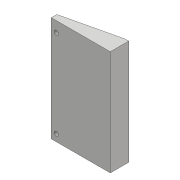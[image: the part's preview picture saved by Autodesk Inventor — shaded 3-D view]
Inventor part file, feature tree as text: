
AUTODESK INVENTOR PART (.ipt)
format: ipt  version: 2018 (Build 220112000, 112)  size: 115,200 bytes
history: native  units: mm
features: sketch x5, extrude x4, hole x1, projected_geometry x1
ambient origin geometry x8: Origin, YZ Plane, XZ Plane, XY Plane, X Axis, Y Axis, Z Axis, Center Point
bodies: Solid1 (feature_tree)
feature tree (11):
  extrude  "Extrusion1"  Depth=30.0mm
  extrude  "Extrusion2"  Depth=43.5mm
  extrude  "Extrusion3"  Depth=1.6mm TaperAngle=0.0deg
  extrude  "Extrusion4"  Depth=2.0mm TaperAngle=0.0deg
  hole  "Hole1"  [1 undecoded]
  sketch  "Sketch1"  dims[d0=55.0mm d1=30.0mm]
  sketch  "Sketch2"  dims[d2=3.0mm d3=0.0mm d4=43.5mm]
  sketch  "Sketch3"  dims[d5=21.5mm d6=1.6mm d7=0.0mm]
  sketch  "Sketch4"  dims[d8=10.0mm d9=2.0mm d10=0.0mm]
  projected_geometry  "Projected Loop1"
  sketch  "Sketch5"  dims[d11=2.0mm d12=0.0mm d13=1.5mm d14=2.0mm d15=2.459mm d16=6.0mm d17=4.0mm d18=2.0mm d19=90.0deg d20=8.0mm d21=20.594885mm]
note: 1 required parameter value undecoded (feature->parameter linkage not recoverable at this tier; creation-order binding heuristic only, values carry confidence <= 0.55)
